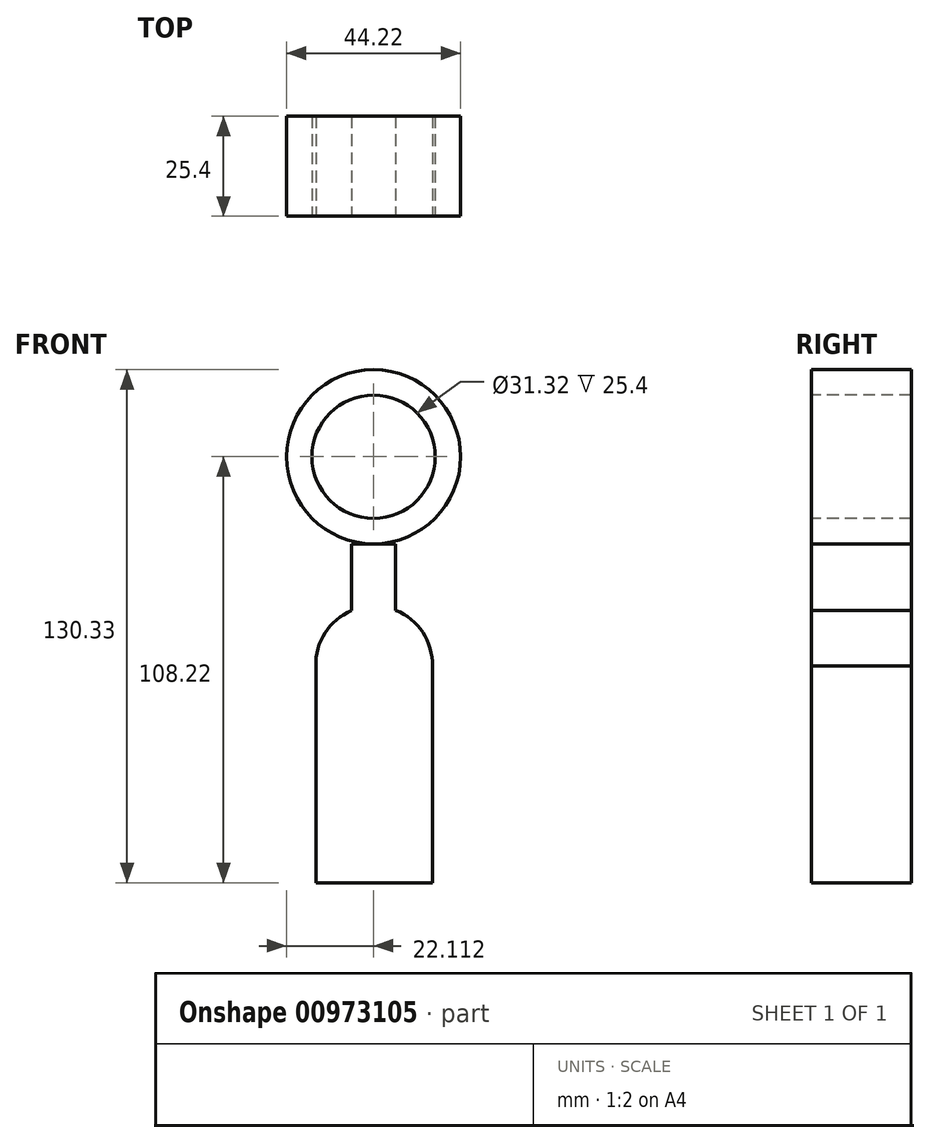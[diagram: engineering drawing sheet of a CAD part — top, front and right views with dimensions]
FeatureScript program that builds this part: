
annotation { "Feature Type Name" : "Feature", "Feature Type Description" : "" }
export const myFeature = defineFeature(function(context is Context, id is Id, definition is map)
    precondition{}
    {
        {
            var Q0;
            Q0=qCreatedBy(makeId("Front.planeOp"),FACE);
            var sketch = newSketch(context, id + "F0", { "sketchPlane" : qUnion([Q0])});
            skLineSegment(sketch, "E0.bottom", {"start": v(0, 0) * mm, "end": v(29.6, 0) * mm});
            skLineSegment(sketch, "E0.left", {"start": v(0, 0) * mm, "end": v(0, 55.47) * mm});
            skLineSegment(sketch, "E0.right", {"start": v(29.6, 0) * mm, "end": v(29.6, 55.47) * mm});
            skArc(sketch, "E1", {"start": v(29.6, 55) * mm, "mid": v(14.8, 70.28) * mm, "end": v(0, 55) * mm});
            skLineSegment(sketch, "E2.top", {"start": v(9.04, 86.11) * mm, "end": v(20.3, 86.11) * mm});
            skLineSegment(sketch, "E2.left", {"start": v(9.04, 69.11) * mm, "end": v(9.04, 86.11) * mm});
            skLineSegment(sketch, "E2.right", {"start": v(20.3, 69.11) * mm, "end": v(20.3, 86.11) * mm});
            skCircle(sketch, "E3", {"center": v(14.67, 108.22) * mm, "radius": 22.11 * mm});
            skPoint(sketch, "E3.centerSnap0", {"position": v(14.67, 86.11) * mm});
            skCircle(sketch, "E4", {"center": v(14.67, 108.22) * mm, "radius": 15.66 * mm});
            skSolve(sketch);
        }
        {
            var Q0;
            {var subQ4=sQuery(id+"F0.wireOp",EDGE,"E2.top");Q0=makeQuery(id+"F0.imprint","IMPRINT",FACE,{"disambiguationData":[TD([[makeQuery(id+"F0.imprint","IMPRINT",EDGE,{"derivedFrom":subQ4}),-1.0]])]});}
            var Q1;
            {var subQ4=sQuery(id+"F0.wireOp",EDGE,"E0.bottom");Q1=makeQuery(id+"F0.imprint","IMPRINT",FACE,{"disambiguationData":[TD([[makeQuery(id+"F0.imprint","IMPRINT",EDGE,{"derivedFrom":subQ4}),1.0]])]});}
            extrude(context, id + "F1", {"entities" : qUnion([Q0, Q1]), "endBound" : BoundingType.SYMMETRIC, "oppositeDirection" : true, "depth" : 25.4 * mm, "offsetDistance" : 25.4 * mm});
        }
        {
            var Q0;
            Q0 = qSketchRegion(id + "F0", true);
            extrude(context, id + "F2", {"entities" : qUnion([Q0]), "operationType" : NewBodyOperationType.ADD, "endBound" : BoundingType.SYMMETRIC, "oppositeDirection" : true, "depth" : 25.4 * mm, "offsetDistance" : 25.4 * mm});
        }
    });
